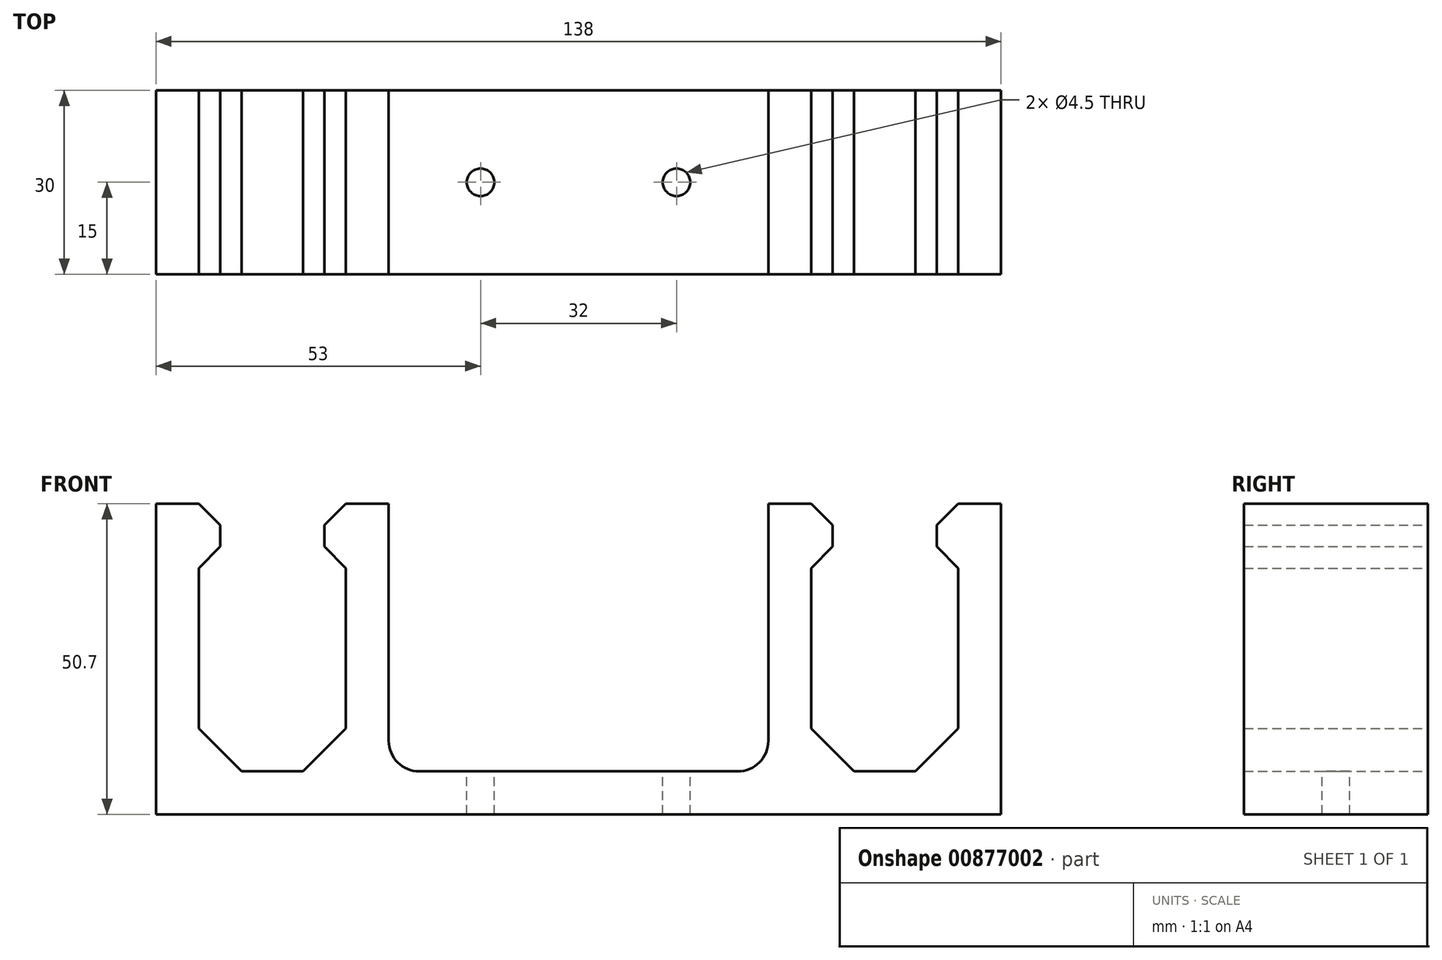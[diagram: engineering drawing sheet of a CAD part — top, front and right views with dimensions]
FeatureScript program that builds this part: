
annotation { "Feature Type Name" : "Feature", "Feature Type Description" : "" }
export const myFeature = defineFeature(function(context is Context, id is Id, definition is map)
    precondition{}
    {
        {
            var Q0;
            Q0=qCreatedBy(makeId("Front.planeOp"),FACE);
            var sketch = newSketch(context, id + "F0", { "sketchPlane" : qUnion([Q0])});
            skLineSegment(sketch, "E0", {"start": v(-12, 13.1) * mm, "end": v(-5, 20.1) * mm});
            skLineSegment(sketch, "E1", {"start": v(-5, 20.1) * mm, "end": v(5, 20.1) * mm});
            skLineSegment(sketch, "E2", {"start": v(5, 20.1) * mm, "end": v(12, 13.1) * mm});
            skLineSegment(sketch, "E3", {"start": v(12, 13.1) * mm, "end": v(12, -13.1) * mm});
            skLineSegment(sketch, "E4", {"start": v(12, -13.1) * mm, "end": v(5, -20.1) * mm});
            skLineSegment(sketch, "E5", {"start": v(5, -20.1) * mm, "end": v(-5, -20.1) * mm});
            skLineSegment(sketch, "E6", {"start": v(-5, -20.1) * mm, "end": v(-12, -13.1) * mm});
            skLineSegment(sketch, "E7", {"start": v(-12, -13.1) * mm, "end": v(-12, 13.1) * mm});
            skPoint(sketch, "E8", {"position": v(-12, 0) * mm});
            skPoint(sketch, "E9", {"position": v(0, 20.1) * mm});
            skLineSegment(sketch, "E10", {"start": v(-8.5, 16.6) * mm, "end": v(-8.5, 20.1) * mm});
            skLineSegment(sketch, "E11", {"start": v(-8.5, 20.1) * mm, "end": v(-12, 23.6) * mm});
            skLineSegment(sketch, "E12", {"start": v(-12, 23.6) * mm, "end": v(-19, 23.6) * mm});
            skLineSegment(sketch, "E13", {"start": v(-19, 23.6) * mm, "end": v(-19, -27.1) * mm});
            skLineSegment(sketch, "E14", {"start": v(-19, -27.1) * mm, "end": v(0, -27.1) * mm});
            skPoint(sketch, "E14.endSnap0", {"position": v(0, -20.1) * mm});
            skLineSegment(sketch, "E15.MirrorCS", {"start": v(19, -27.1) * mm, "end": v(0, -27.1) * mm});
            skLineSegment(sketch, "E16.MirrorCS", {"start": v(19, 23.6) * mm, "end": v(19, -15.1) * mm});
            skLineSegment(sketch, "E17.MirrorCS", {"start": v(12, 23.6) * mm, "end": v(19, 23.6) * mm});
            skLineSegment(sketch, "E18.MirrorCS", {"start": v(8.5, 20.1) * mm, "end": v(12, 23.6) * mm});
            skLineSegment(sketch, "E19.MirrorCS", {"start": v(8.5, 16.6) * mm, "end": v(8.5, 20.1) * mm});
            skLineSegment(sketch, "E20.1.0.0", {"start": v(112, 13.1) * mm, "end": v(112, -13.1) * mm});
            skLineSegment(sketch, "E20.1.0.1", {"start": v(88, 23.6) * mm, "end": v(81, 23.6) * mm});
            skLineSegment(sketch, "E20.1.0.2", {"start": v(112, 23.6) * mm, "end": v(119, 23.6) * mm});
            skLineSegment(sketch, "E20.1.0.3", {"start": v(91.5, 20.1) * mm, "end": v(88, 23.6) * mm});
            skPoint(sketch, "E20.1.0.4", {"position": v(88, 0) * mm});
            skLineSegment(sketch, "E20.1.0.5", {"start": v(95, -20.1) * mm, "end": v(88, -13.1) * mm});
            skLineSegment(sketch, "E20.1.0.6", {"start": v(108.5, 16.6) * mm, "end": v(108.5, 20.1) * mm});
            skLineSegment(sketch, "E20.1.0.7", {"start": v(112, -13.1) * mm, "end": v(105, -20.1) * mm});
            skLineSegment(sketch, "E20.1.0.8", {"start": v(108.5, 20.1) * mm, "end": v(112, 23.6) * mm});
            skPoint(sketch, "E20.1.0.9", {"position": v(100, -20.1) * mm});
            skLineSegment(sketch, "E20.1.0.10", {"start": v(119, -27.1) * mm, "end": v(100, -27.1) * mm});
            skLineSegment(sketch, "E20.1.0.11", {"start": v(105, -20.1) * mm, "end": v(95, -20.1) * mm});
            skLineSegment(sketch, "E20.1.0.12", {"start": v(81, -27.1) * mm, "end": v(100, -27.1) * mm});
            skLineSegment(sketch, "E20.1.0.13", {"start": v(119, 23.6) * mm, "end": v(119, -27.1) * mm});
            skLineSegment(sketch, "E20.1.0.14", {"start": v(88, -13.1) * mm, "end": v(88, 13.1) * mm});
            skLineSegment(sketch, "E20.1.0.15", {"start": v(91.5, 16.6) * mm, "end": v(91.5, 20.1) * mm});
            skPoint(sketch, "E20.1.0.16", {"position": v(100, 20.1) * mm});
            skLineSegment(sketch, "E20.1.0.17", {"start": v(105, 20.1) * mm, "end": v(112, 13.1) * mm});
            skLineSegment(sketch, "E20.1.0.18", {"start": v(81, 23.6) * mm, "end": v(81, -15.1) * mm});
            skLineSegment(sketch, "E20.1.0.19", {"start": v(88, 13.1) * mm, "end": v(95, 20.1) * mm});
            skLineSegment(sketch, "E20.1.0.20", {"start": v(95, 20.1) * mm, "end": v(105, 20.1) * mm});
            skLineSegment(sketch, "E20.direction1", {"start": v(-19, -27.1) * mm, "end": v(81, -27.1) * mm, "construction": true});
            skLineSegment(sketch, "E21", {"start": v(19, -27.1) * mm, "end": v(81, -27.1) * mm});
            skLineSegment(sketch, "E22", {"start": v(24, -20.1) * mm, "end": v(76, -20.1) * mm});
            skPoint(sketch, "E23.newPointA", {"position": v(19, -20.1) * mm});
            skPoint(sketch, "E23.newPointB", {"position": v(19, -27.1) * mm});
            skArc(sketch, "E23.filletArc", {"start": v(19, -15.1) * mm, "mid": v(20.46, -18.64) * mm, "end": v(24, -20.1) * mm});
            skPoint(sketch, "E24.newPointB", {"position": v(81, -27.1) * mm});
            skArc(sketch, "E24.filletArc", {"start": v(76, -20.1) * mm, "mid": v(79.54, -18.64) * mm, "end": v(81, -15.1) * mm});
            skSolve(sketch);
        }
        {
            var Q0;
            {var subQ2=sQuery(id+"F0.wireOp",EDGE,"E3");Q0=makeQuery(id+"F0.imprint","IMPRINT",FACE,{"disambiguationData":[TD([[makeQuery(id+"F0.imprint","IMPRINT",EDGE,{"derivedFrom":subQ2}),1.0]])]});}
            extrude(context, id + "F1", {"entities" : qUnion([Q0]), "depth" : 30 * mm, "offsetDistance" : 25 * mm});
        }
        {
            var Q0;
            Q0=makeQuery(id+"F1.opExtrude","SWEPT_FACE",FACE,{"disambiguationData":[OSD([sQuery(id+"F0.wireOp",EDGE,"E22")])]});
            var sketch = newSketch(context, id + "F2", { "sketchPlane" : qUnion([Q0])});
            skPoint(sketch, "E25", {"position": v(24, -15) * mm});
            skCircle(sketch, "E26", {"center": v(34, -15) * mm, "radius": 2.25 * mm});
            skCircle(sketch, "E27", {"center": v(66, -15) * mm, "radius": 2.25 * mm});
            skSolve(sketch);
        }
        {
            var Q0;
            Q0=makeQuery(id+"F2.imprint","IMPRINT",FACE,{"disambiguationData":[TD([[makeQuery(id+"F2.imprint","IMPRINT",EDGE,{"derivedFrom":sQuery(id+"F2.wireOp",EDGE,"E26")}),1.0]])]});
            var Q1;
            Q1=makeQuery(id+"F2.imprint","IMPRINT",FACE,{"disambiguationData":[TD([[makeQuery(id+"F2.imprint","IMPRINT",EDGE,{"derivedFrom":sQuery(id+"F2.wireOp",EDGE,"E27")}),1.0]])]});
            var Q2;
            Q2=makeQuery(id+"F1.opExtrude","SWEPT_FACE",FACE,{"disambiguationData":[OSD([sQuery(id+"F0.wireOp",EDGE,"E14"),sQuery(id+"F0.wireOp",EDGE,"E15.MirrorCS"),sQuery(id+"F0.wireOp",EDGE,"E20.1.0.10"),sQuery(id+"F0.wireOp",EDGE,"E20.1.0.12"),sQuery(id+"F0.wireOp",EDGE,"E21")])]});
            extrude(context, id + "F3", {"entities" : qUnion([Q0, Q1]), "operationType" : NewBodyOperationType.REMOVE, "endBound" : BoundingType.UP_TO_SURFACE, "oppositeDirection" : true, "depth" : 25 * mm, "endBoundEntityFace" : qUnion([Q2]), "offsetDistance" : 25 * mm});
        }
    });
